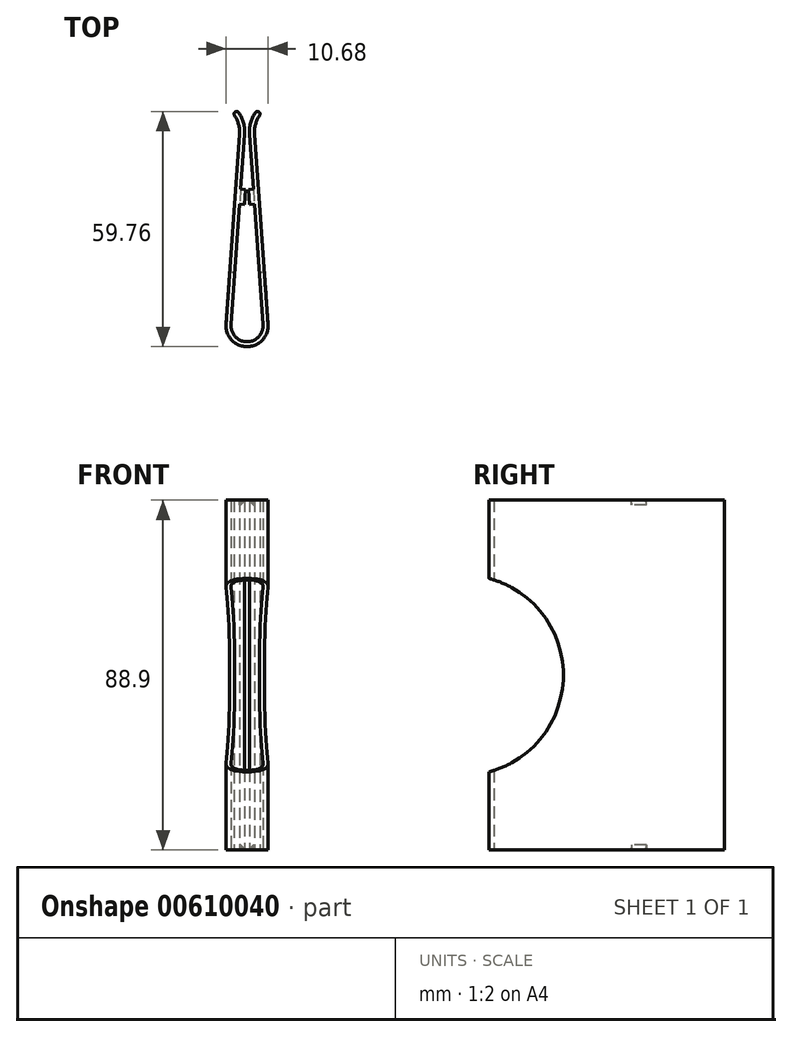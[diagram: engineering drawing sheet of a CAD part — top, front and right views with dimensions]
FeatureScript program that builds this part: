
annotation { "Feature Type Name" : "Feature", "Feature Type Description" : "" }
export const myFeature = defineFeature(function(context is Context, id is Id, definition is map)
    precondition{}
    {
        {
            var Q0;
            Q0=qCreatedBy(makeId("Top.planeOp"),FACE);
            var sketch = newSketch(context, id + "F0", { "sketchPlane" : qUnion([Q0])});
            skLineSegment(sketch, "E0", {"start": v(0, 0) * mm, "end": v(0, 48.26) * mm, "construction": true});
            skLineSegment(sketch, "E1", {"start": v(0.63, 48.26) * mm, "end": v(-0.64, 48.26) * mm, "construction": true});
            skPoint(sketch, "E2", {"position": v(0, 0) * mm});
            skLineSegment(sketch, "E3", {"start": v(4.06, 0) * mm, "end": v(-4.06, 0) * mm, "construction": true});
            skLineSegment(sketch, "E4", {"start": v(-0.64, 48.26) * mm, "end": v(-4.06, 0) * mm});
            skLineSegment(sketch, "E5", {"start": v(0.63, 48.26) * mm, "end": v(4.06, 0) * mm});
            skArc(sketch, "E6", {"start": v(-4.06, 0) * mm, "mid": v(0, -4.36) * mm, "end": v(4.06, 0) * mm});
            skArc(sketch, "E7", {"start": v(-0.64, 48.26) * mm, "mid": v(-0.91, 51.18) * mm, "end": v(-2.12, 53.85) * mm});
            skArc(sketch, "E8", {"start": v(2.12, 53.85) * mm, "mid": v(0.91, 51.18) * mm, "end": v(0.63, 48.26) * mm});
            skArc(sketch, "E9.0", {"start": v(3.18, 53.14) * mm, "mid": v(2.14, 50.85) * mm, "end": v(1.9, 48.35) * mm});
            skArc(sketch, "E9.1", {"start": v(-1.9, 48.35) * mm, "mid": v(-2.14, 50.85) * mm, "end": v(-3.18, 53.14) * mm});
            skLineSegment(sketch, "E9.2", {"start": v(-1.9, 48.35) * mm, "end": v(-5.33, 0.1) * mm});
            skArc(sketch, "E9.3", {"start": v(-5.33, 0.1) * mm, "mid": v(0, -5.63) * mm, "end": v(5.33, 0.1) * mm});
            skLineSegment(sketch, "E9.4", {"start": v(1.9, 48.35) * mm, "end": v(5.33, 0.1) * mm});
            skArc(sketch, "E10", {"start": v(-2.12, 53.85) * mm, "mid": v(-3, 54.02) * mm, "end": v(-3.18, 53.14) * mm});
            skArc(sketch, "E11", {"start": v(3.18, 53.14) * mm, "mid": v(3, 54.02) * mm, "end": v(2.12, 53.85) * mm});
            skSolve(sketch);
        }
        {
            var Q0;
            Q0=makeQuery(id+"F0.imprint","IMPRINT",FACE,{"disambiguationData":[TD([[makeQuery(id+"F0.imprint","IMPRINT",EDGE,{"derivedFrom":sQuery(id+"F0.wireOp",EDGE,"E4")}),-1.0]])]});
            extrude(context, id + "F1", {"entities" : qUnion([Q0]), "depth" : 88.9 * mm, "offsetDistance" : 25.4 * mm});
        }
        {
            var Q0;
            Q0=makeQuery(id+"F1.opExtrude","CAP_FACE",FACE,{"disambiguationData":[OSD([sQuery(id+"F0.wireOp",EDGE,"E4"),sQuery(id+"F0.wireOp",EDGE,"E5"),sQuery(id+"F0.wireOp",EDGE,"E6"),sQuery(id+"F0.wireOp",EDGE,"E7"),sQuery(id+"F0.wireOp",EDGE,"E8"),sQuery(id+"F0.wireOp",EDGE,"E9.0"),sQuery(id+"F0.wireOp",EDGE,"E9.1"),sQuery(id+"F0.wireOp",EDGE,"E9.2"),sQuery(id+"F0.wireOp",EDGE,"E9.3"),sQuery(id+"F0.wireOp",EDGE,"E9.4"),sQuery(id+"F0.wireOp",EDGE,"E10"),sQuery(id+"F0.wireOp",EDGE,"E11")])],"isStart":false});
            var sketch = newSketch(context, id + "F2", { "sketchPlane" : qUnion([Q0])});
            skLineSegment(sketch, "E12", {"start": v(-1.62, 34.37) * mm, "end": v(-0.36, 34.28) * mm});
            skLineSegment(sketch, "E13", {"start": v(-0.36, 34.28) * mm, "end": v(-0.63, 30.48) * mm});
            skLineSegment(sketch, "E14", {"start": v(-0.63, 30.48) * mm, "end": v(-1.9, 30.57) * mm});
            skLineSegment(sketch, "E15", {"start": v(1.62, 34.37) * mm, "end": v(0.36, 34.28) * mm});
            skLineSegment(sketch, "E16", {"start": v(0.36, 34.28) * mm, "end": v(0.63, 30.48) * mm});
            skLineSegment(sketch, "E17", {"start": v(0.63, 30.48) * mm, "end": v(1.9, 30.57) * mm});
            skSolve(sketch);
        }
        {
            var Q0;
            Q0 = qSketchRegion(id + "F2", true);
            var Q1;
            {var subQ0=sQuery(id+"F2.wireOp",EDGE,"E12");Q1=makeQuery(id+"F2.imprint","IMPRINT",FACE,{"disambiguationData":[TD([[makeQuery(id+"F2.imprint","IMPRINT",EDGE,{"derivedFrom":subQ0}),-1.0]])]});}
            var Q2;
            {var subQ0=sQuery(id+"F2.wireOp",EDGE,"E15");Q2=makeQuery(id+"F2.imprint","IMPRINT",FACE,{"disambiguationData":[TD([[makeQuery(id+"F2.imprint","IMPRINT",EDGE,{"derivedFrom":subQ0}),1.0]])]});}
            extrude(context, id + "F3", {"entities" : qUnion([Q0, Q1, Q2]), "operationType" : NewBodyOperationType.ADD, "oppositeDirection" : true, "depth" : 1.27 * mm, "offsetDistance" : 25.4 * mm});
        }
        {
            var Q0;
            Q0=makeQuery(id+"F1.opExtrude","CAP_FACE",FACE,{"disambiguationData":[OSD([sQuery(id+"F0.wireOp",EDGE,"E4"),sQuery(id+"F0.wireOp",EDGE,"E5"),sQuery(id+"F0.wireOp",EDGE,"E6"),sQuery(id+"F0.wireOp",EDGE,"E7"),sQuery(id+"F0.wireOp",EDGE,"E8"),sQuery(id+"F0.wireOp",EDGE,"E9.0"),sQuery(id+"F0.wireOp",EDGE,"E9.1"),sQuery(id+"F0.wireOp",EDGE,"E9.2"),sQuery(id+"F0.wireOp",EDGE,"E9.3"),sQuery(id+"F0.wireOp",EDGE,"E9.4"),sQuery(id+"F0.wireOp",EDGE,"E10"),sQuery(id+"F0.wireOp",EDGE,"E11")])],"isStart":true});
            var sketch = newSketch(context, id + "F4", { "sketchPlane" : qUnion([Q0])});
            skLineSegment(sketch, "E18", {"start": v(-1.9, -30.57) * mm, "end": v(-0.63, -30.48) * mm});
            skLineSegment(sketch, "E19", {"start": v(-0.63, -30.48) * mm, "end": v(-0.36, -34.28) * mm});
            skLineSegment(sketch, "E20", {"start": v(-0.36, -34.28) * mm, "end": v(-1.62, -34.37) * mm});
            skLineSegment(sketch, "E21", {"start": v(1.62, -34.37) * mm, "end": v(0.36, -34.28) * mm});
            skLineSegment(sketch, "E22", {"start": v(0.36, -34.28) * mm, "end": v(0.63, -30.48) * mm});
            skLineSegment(sketch, "E23", {"start": v(0.63, -30.48) * mm, "end": v(1.9, -30.57) * mm});
            skSolve(sketch);
        }
        {
            var Q0;
            {var subQ0=sQuery(id+"F4.wireOp",EDGE,"E18");Q0=makeQuery(id+"F4.imprint","IMPRINT",FACE,{"disambiguationData":[TD([[makeQuery(id+"F4.imprint","IMPRINT",EDGE,{"derivedFrom":subQ0}),-1.0]])]});}
            var Q1;
            {var subQ0=sQuery(id+"F4.wireOp",EDGE,"E21");Q1=makeQuery(id+"F4.imprint","IMPRINT",FACE,{"disambiguationData":[TD([[makeQuery(id+"F4.imprint","IMPRINT",EDGE,{"derivedFrom":subQ0}),-1.0]])]});}
            extrude(context, id + "F5", {"entities" : qUnion([Q0, Q1]), "operationType" : NewBodyOperationType.ADD, "oppositeDirection" : true, "depth" : 1.27 * mm, "offsetDistance" : 25.4 * mm});
        }
        {
            var Q0;
            Q0=makeQuery(id+"F5.opExtrude","CAP_EDGE",EDGE,{"disambiguationData":[OSD([sQuery(id+"F4.wireOp",EDGE,"E19")])],"isStart":false});
            var Q1;
            Q1=makeQuery(id+"F5.opExtrude","CAP_EDGE",EDGE,{"disambiguationData":[OSD([sQuery(id+"F4.wireOp",EDGE,"E22")])],"isStart":false});
            var Q2;
            Q2=makeQuery(id+"F3.opExtrude","CAP_EDGE",EDGE,{"disambiguationData":[OSD([sQuery(id+"F2.wireOp",EDGE,"E13")])],"isStart":false});
            var Q3;
            Q3=makeQuery(id+"F3.opExtrude","CAP_EDGE",EDGE,{"disambiguationData":[OSD([sQuery(id+"F2.wireOp",EDGE,"E16")])],"isStart":false});
            chamfer(context, id + "F6", {"entities" : qUnion([Q0, Q1, Q2, Q3]), "width" : 1.27 * mm, "tangentPropagation" : true});
        }
        {
            var Q0;
            Q0=qCreatedBy(makeId("Right.planeOp"),FACE);
            var sketch = newSketch(context, id + "F7", { "sketchPlane" : qUnion([Q0])});
            skLineSegment(sketch, "E24", {"start": v(0, 0) * mm, "end": v(0, 88.9) * mm, "construction": true});
            skLineSegment(sketch, "E25.right", {"start": v(-5.84, 69.07) * mm, "end": v(-5.84, 19.83) * mm});
            skPoint(sketch, "E25.middle", {"position": v(0, 44.45) * mm});
            skLineSegment(sketch, "E26", {"start": v(-5.84, 0) * mm, "end": v(-5.84, 88.9) * mm, "construction": true});
            skArc(sketch, "E27", {"start": v(-5.84, 19.83) * mm, "mid": v(13.33, 44.45) * mm, "end": v(-5.84, 69.07) * mm});
            skLineSegment(sketch, "E28", {"start": v(0, 44.45) * mm, "end": v(-12.07, 44.45) * mm, "construction": true});
            skSolve(sketch);
        }
        {
            var Q0;
            Q0 = qSketchRegion(id + "F7", true);
            extrude(context, id + "F8", {"entities" : qUnion([Q0]), "operationType" : NewBodyOperationType.REMOVE, "endBound" : BoundingType.SYMMETRIC, "oppositeDirection" : true, "depth" : 25.4 * mm, "offsetDistance" : 25.4 * mm});
        }
        {
            var Q0;
            Q0=qCreatedBy(makeId("Front.planeOp"),FACE);
            cPlane(context, id + "F9", {"entities" : qUnion([Q0]), "cplaneType" : CPlaneType.OFFSET, "offset" : 51.43 * mm, "oppositeDirection" : true, "width" : 152.4 * mm, "height" : 152.4 * mm});
        }
    });
